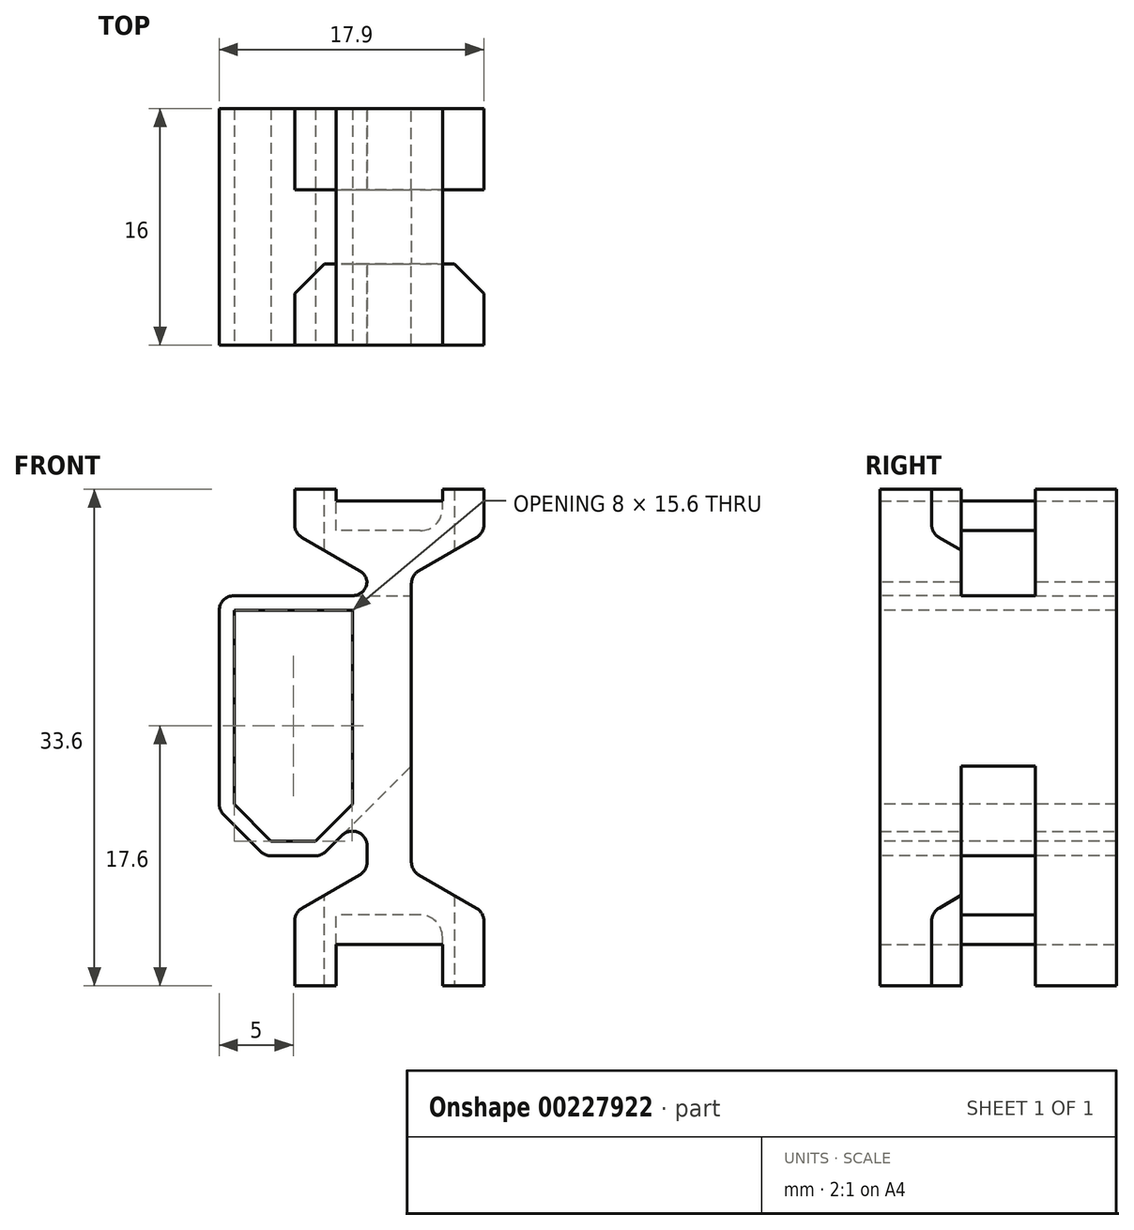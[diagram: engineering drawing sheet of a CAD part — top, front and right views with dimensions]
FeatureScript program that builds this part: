
annotation { "Feature Type Name" : "Feature", "Feature Type Description" : "" }
export const myFeature = defineFeature(function(context is Context, id is Id, definition is map)
    precondition{}
    {
        {
            var Q0;
            Q0=qCreatedBy(makeId("Front.planeOp"),FACE);
            var sketch = newSketch(context, id + "F0", { "sketchPlane" : qUnion([Q0])});
            skLineSegment(sketch, "E0.bottom", {"start": v(-6.4, 30.8) * mm, "end": v(-3.6, 30.8) * mm});
            skLineSegment(sketch, "E0.top", {"start": v(-6.4, -2.8) * mm, "end": v(-3.6, -2.8) * mm});
            skLineSegment(sketch, "E0.left", {"start": v(-6.4, 30.8) * mm, "end": v(-6.4, 27.83) * mm});
            skLineSegment(sketch, "E0.right", {"start": v(-3.6, 30.8) * mm, "end": v(-3.6, 30) * mm});
            skLineSegment(sketch, "E1.bottom", {"start": v(3.6, 30.8) * mm, "end": v(6.4, 30.8) * mm});
            skLineSegment(sketch, "E1.top", {"start": v(3.6, -2.8) * mm, "end": v(6.4, -2.8) * mm});
            skLineSegment(sketch, "E1.left", {"start": v(3.6, 30.8) * mm, "end": v(3.6, 30) * mm});
            skLineSegment(sketch, "E1.right", {"start": v(6.4, 30.8) * mm, "end": v(6.4, 27.83) * mm});
            skLineSegment(sketch, "E2.bottom", {"start": v(-3.6, 0) * mm, "end": v(3.6, 0) * mm});
            skLineSegment(sketch, "E2.top", {"start": v(-3.6, 30) * mm, "end": v(3.6, 30) * mm});
            skPoint(sketch, "E3", {"position": v(-5, 30.8) * mm});
            skPoint(sketch, "E4", {"position": v(5, 30.8) * mm});
            skLineSegment(sketch, "E5.trimOffspring", {"start": v(-6.4, 2.17) * mm, "end": v(-6.4, -2.8) * mm});
            skLineSegment(sketch, "E6.trimOffspring", {"start": v(-3.6, 0) * mm, "end": v(-3.6, -2.8) * mm});
            skLineSegment(sketch, "E7.trimOffspring", {"start": v(3.6, 0) * mm, "end": v(3.6, -2.8) * mm});
            skLineSegment(sketch, "E8", {"start": v(0, 30) * mm, "end": v(0, 0) * mm, "construction": true});
            skLineSegment(sketch, "E9", {"start": v(6.4, 15) * mm, "end": v(0, 15) * mm, "construction": true});
            skLineSegment(sketch, "E10", {"start": v(-6.4, 27.83) * mm, "end": v(-1.5, 25) * mm});
            skLineSegment(sketch, "E11", {"start": v(-1.5, 25) * mm, "end": v(-1.5, 5) * mm});
            skLineSegment(sketch, "E12", {"start": v(-1.5, 5) * mm, "end": v(-6.4, 2.17) * mm});
            skLineSegment(sketch, "E13.MirrorCS", {"start": v(1.5, 5) * mm, "end": v(6.4, 2.17) * mm});
            skLineSegment(sketch, "E14.MirrorCS", {"start": v(6.4, 27.83) * mm, "end": v(1.5, 25) * mm});
            skLineSegment(sketch, "E15.MirrorCS", {"start": v(1.5, 25) * mm, "end": v(1.5, 5) * mm});
            skLineSegment(sketch, "E16.trimOffspring", {"start": v(6.4, 2.17) * mm, "end": v(6.4, -2.8) * mm});
            skSolve(sketch);
        }
        {
            var Q0;
            Q0 = qSketchRegion(id + "F0", true);
            extrude(context, id + "F1", {"entities" : qUnion([Q0]), "depth" : 16 * mm});
        }
        {
            var Q0;
            Q0=makeQuery(id+"F1.opExtrude","SWEPT_FACE",FACE,{"disambiguationData":[OSD([sQuery(id+"F0.wireOp",EDGE,"E0.bottom")])]});
            var sketch = newSketch(context, id + "F2", { "sketchPlane" : qUnion([Q0])});
            skLineSegment(sketch, "E17", {"start": v(-6.4, -8) * mm, "end": v(6.4, -8) * mm, "construction": true});
            skLineSegment(sketch, "E18.0.1", {"start": v(-6.4, -5.5) * mm, "end": v(-6.4, -10.5) * mm});
            skLineSegment(sketch, "E18.0.3", {"start": v(-3.6, -10.5) * mm, "end": v(-3.6, -5.5) * mm});
            skLineSegment(sketch, "E19.0.1", {"start": v(3.6, -5.5) * mm, "end": v(3.6, -10.5) * mm});
            skLineSegment(sketch, "E19.0.3", {"start": v(6.4, -10.5) * mm, "end": v(6.4, -5.5) * mm});
            skLineSegment(sketch, "E20", {"start": v(-6.4, -5.5) * mm, "end": v(-3.6, -5.5) * mm});
            skLineSegment(sketch, "E21.MirrorCS", {"start": v(-6.4, -10.5) * mm, "end": v(-3.6, -10.5) * mm});
            skLineSegment(sketch, "E22.trimOffspring", {"start": v(3.6, -5.5) * mm, "end": v(6.4, -5.5) * mm});
            skLineSegment(sketch, "E23.trimOffspring", {"start": v(3.6, -10.5) * mm, "end": v(6.4, -10.5) * mm});
            skSolve(sketch);
        }
        {
            var Q0;
            Q0=makeQuery(id+"F2.imprint","IMPRINT",FACE,{"disambiguationData":[TD([[makeQuery(id+"F2.imprint","IMPRINT",EDGE,{"derivedFrom":sQuery(id+"F2.wireOp",EDGE,"E18.0.1")}),-1.0]])]});
            var Q1;
            Q1=makeQuery(id+"F2.imprint","IMPRINT",FACE,{"disambiguationData":[TD([[makeQuery(id+"F2.imprint","IMPRINT",EDGE,{"derivedFrom":sQuery(id+"F2.wireOp",EDGE,"E19.0.1")}),1.0]])]});
            extrude(context, id + "F3", {"entities" : qUnion([Q0, Q1]), "operationType" : NewBodyOperationType.REMOVE, "endBound" : BoundingType.THROUGH_ALL, "oppositeDirection" : true, "depth" : 25 * mm});
        }
        {
            var Q0;
            Q0=makeQuery(id+"F3.boolean.opBoolean","COPY",FACE,{"disambiguationData":[TD([makeQuery(id+"F1.opExtrude","SWEPT_FACE",FACE,{"disambiguationData":[OSD([sQuery(id+"F0.wireOp",EDGE,"E2.bottom")])]})])],"derivedFrom":makeQuery(id+"F3.opExtrude","SWEPT_FACE",FACE,{"disambiguationData":[OSD([sQuery(id+"F2.wireOp",EDGE,"E18.0.3")])]})});
            var sketch = newSketch(context, id + "F4", { "sketchPlane" : qUnion([Q0])});
            skLineSegment(sketch, "E24.bottom", {"start": v(5.5, 2) * mm, "end": v(10.5, 2) * mm});
            skLineSegment(sketch, "E24.top", {"start": v(5.5, 28) * mm, "end": v(10.5, 28) * mm});
            skLineSegment(sketch, "E24.left", {"start": v(5.5, 2) * mm, "end": v(5.5, 28) * mm});
            skLineSegment(sketch, "E24.right", {"start": v(10.5, 2) * mm, "end": v(10.5, 28) * mm});
            skSolve(sketch);
        }
        {
            var Q0;
            Q0 = qSketchRegion(id + "F4", true);
            extrude(context, id + "F5", {"entities" : qUnion([Q0]), "operationType" : NewBodyOperationType.REMOVE, "endBound" : BoundingType.THROUGH_ALL, "oppositeDirection" : true, "depth" : 25 * mm});
        }
        {
            var Q0;
            Q0=makeQuery(id+"F1.opExtrude","CAP_FACE",FACE,{"disambiguationData":[OSD([sQuery(id+"F0.wireOp",EDGE,"E0.bottom"),sQuery(id+"F0.wireOp",EDGE,"E0.top"),sQuery(id+"F0.wireOp",EDGE,"E0.left"),sQuery(id+"F0.wireOp",EDGE,"E0.right"),sQuery(id+"F0.wireOp",EDGE,"E1.bottom"),sQuery(id+"F0.wireOp",EDGE,"E1.top"),sQuery(id+"F0.wireOp",EDGE,"E1.left"),sQuery(id+"F0.wireOp",EDGE,"E1.right"),sQuery(id+"F0.wireOp",EDGE,"E2.bottom"),sQuery(id+"F0.wireOp",EDGE,"E2.top"),sQuery(id+"F0.wireOp",EDGE,"E5.trimOffspring"),sQuery(id+"F0.wireOp",EDGE,"E6.trimOffspring"),sQuery(id+"F0.wireOp",EDGE,"E7.trimOffspring"),sQuery(id+"F0.wireOp",EDGE,"XNyugLao-tsnu-Sah3-VUFn-nM4j8uXXMLVh"),sQuery(id+"F0.wireOp",EDGE,"qag7rgW7-rpCx-CGtA-zPlC-gOamsbcd0Z1q"),sQuery(id+"F0.wireOp",EDGE,"LMqOLITl-EVo5-MTzV-QNNo-kao2bXQrC091"),sQuery(id+"F0.wireOp",EDGE,"kiGqG5in-MVmp-Csza-V1P0-bwSz3CtIkC7l")])],"isStart":false});
            var sketch = newSketch(context, id + "F6", { "sketchPlane" : qUnion([Q0])});
            skLineSegment(sketch, "E25", {"start": v(-10.5, 22.6) * mm, "end": v(-10.5, 9.5) * mm});
            skLineSegment(sketch, "E26", {"start": v(-10.5, 9.5) * mm, "end": v(-8, 7) * mm});
            skLineSegment(sketch, "E27", {"start": v(-8, 7) * mm, "end": v(-5, 7) * mm});
            skLineSegment(sketch, "E28", {"start": v(-6.5, 7) * mm, "end": v(-6.5, 22.6) * mm, "construction": true});
            skLineSegment(sketch, "E29.0", {"start": v(-4.59, 6) * mm, "end": v(1.5, 12.09) * mm});
            skLineSegment(sketch, "E29.1", {"start": v(-11.5, 23.6) * mm, "end": v(-11.5, 23.6) * mm});
            skLineSegment(sketch, "E29.2", {"start": v(-11.5, 23.6) * mm, "end": v(-11.5, 9.09) * mm});
            skLineSegment(sketch, "E29.3", {"start": v(-11.5, 9.09) * mm, "end": v(-8.41, 6) * mm});
            skLineSegment(sketch, "E29.4", {"start": v(-8.41, 6) * mm, "end": v(-4.59, 6) * mm});
            skLineSegment(sketch, "E30", {"start": v(-11.5, 23.6) * mm, "end": v(1.5, 23.6) * mm});
            skLineSegment(sketch, "E31", {"start": v(1.5, 12.09) * mm, "end": v(1.5, 23.6) * mm});
            skLineSegment(sketch, "E32.MirrorCS", {"start": v(-2.5, 9.5) * mm, "end": v(-5, 7) * mm});
            skLineSegment(sketch, "E33.MirrorCS", {"start": v(-2.5, 22.6) * mm, "end": v(-2.5, 9.5) * mm});
            skLineSegment(sketch, "E34", {"start": v(-10.5, 22.6) * mm, "end": v(-2.5, 22.6) * mm});
            skSolve(sketch);
        }
        {
            var Q0;
            Q0 = qSketchRegion(id + "F6", true);
            var Q1;
            Q1=makeQuery(id+"F1.opExtrude","CAP_FACE",FACE,{"disambiguationData":[OSD([sQuery(id+"F0.wireOp",EDGE,"E0.bottom"),sQuery(id+"F0.wireOp",EDGE,"E0.top"),sQuery(id+"F0.wireOp",EDGE,"E0.left"),sQuery(id+"F0.wireOp",EDGE,"E0.right"),sQuery(id+"F0.wireOp",EDGE,"E1.bottom"),sQuery(id+"F0.wireOp",EDGE,"E1.top"),sQuery(id+"F0.wireOp",EDGE,"E1.left"),sQuery(id+"F0.wireOp",EDGE,"E1.right"),sQuery(id+"F0.wireOp",EDGE,"E2.bottom"),sQuery(id+"F0.wireOp",EDGE,"E2.top"),sQuery(id+"F0.wireOp",EDGE,"E5.trimOffspring"),sQuery(id+"F0.wireOp",EDGE,"E6.trimOffspring"),sQuery(id+"F0.wireOp",EDGE,"E7.trimOffspring"),sQuery(id+"F0.wireOp",EDGE,"XNyugLao-tsnu-Sah3-VUFn-nM4j8uXXMLVh"),sQuery(id+"F0.wireOp",EDGE,"qag7rgW7-rpCx-CGtA-zPlC-gOamsbcd0Z1q"),sQuery(id+"F0.wireOp",EDGE,"LMqOLITl-EVo5-MTzV-QNNo-kao2bXQrC091"),sQuery(id+"F0.wireOp",EDGE,"kiGqG5in-MVmp-Csza-V1P0-bwSz3CtIkC7l")])],"isStart":true});
            extrude(context, id + "F7", {"entities" : qUnion([Q0]), "operationType" : NewBodyOperationType.ADD, "endBound" : BoundingType.UP_TO_SURFACE, "oppositeDirection" : true, "endBoundEntityFace" : qUnion([Q1]), "depth" : 25 * mm});
        }
        {
            var Q0;
            Q0=makeQuery(id+"F5.boolean.opBoolean","INTERSECT",EDGE,{"derivedFrom":[makeQuery(id+"F3.boolean.opBoolean","COPY",FACE,{"disambiguationData":[TD([makeQuery(id+"F1.opExtrude","SWEPT_FACE",FACE,{"disambiguationData":[OSD([sQuery(id+"F0.wireOp",EDGE,"E2.bottom")])]})])],"derivedFrom":makeQuery(id+"F3.opExtrude","SWEPT_FACE",FACE,{"disambiguationData":[OSD([sQuery(id+"F2.wireOp",EDGE,"E19.0.1")])]})}),makeQuery(id+"F5.opExtrude","SWEPT_FACE",FACE,{"disambiguationData":[OSD([sQuery(id+"F4.wireOp",EDGE,"E24.bottom")])]})]});
            var Q1;
            Q1=makeQuery(id+"F5.boolean.opBoolean","INTERSECT",EDGE,{"derivedFrom":[makeQuery(id+"F3.boolean.opBoolean","COPY",FACE,{"disambiguationData":[TD([makeQuery(id+"F1.opExtrude","SWEPT_FACE",FACE,{"disambiguationData":[OSD([sQuery(id+"F0.wireOp",EDGE,"E1.left")])]})])],"derivedFrom":makeQuery(id+"F3.opExtrude","SWEPT_FACE",FACE,{"disambiguationData":[OSD([sQuery(id+"F2.wireOp",EDGE,"E19.0.1")])]})}),makeQuery(id+"F5.opExtrude","SWEPT_FACE",FACE,{"disambiguationData":[OSD([sQuery(id+"F4.wireOp",EDGE,"E24.top")])]})]});
            var Q2;
            Q2=makeQuery(id+"F5.boolean.opBoolean","COPY",EDGE,{"derivedFrom":makeQuery(id+"F5.opExtrude","CAP_EDGE",EDGE,{"disambiguationData":[OSD([sQuery(id+"F4.wireOp",EDGE,"E24.top")])],"isStart":true})});
            var Q3;
            Q3=makeQuery(id+"F5.boolean.opBoolean","COPY",EDGE,{"derivedFrom":makeQuery(id+"F5.opExtrude","CAP_EDGE",EDGE,{"disambiguationData":[OSD([sQuery(id+"F4.wireOp",EDGE,"E24.bottom")])],"isStart":true})});
            fillet(context, id + "F8", {"entities" : qUnion([Q0, Q1, Q2, Q3]), "radius" : 1.5 * mm, "tangentPropagation" : true, "allowEdgeOverflow" : false});
        }
        {
            var Q0;
            {var subQ0=sQuery(id+"F2.wireOp",EDGE,"E23.trimOffspring");Q0=makeQuery(id+"F3.boolean.opBoolean","COPY",EDGE,{"disambiguationData":[TD([makeQuery(id+"F1.opExtrude","SWEPT_FACE",FACE,{"disambiguationData":[OSD([sQuery(id+"F0.wireOp",EDGE,"E1.top")])]})])],"derivedFrom":makeQuery(id+"F3.opExtrude","SWEPT_EDGE",EDGE,{"disambiguationData":[OSD([sQuery(id+"F2.wireOp",EDGE,"E19.0.3"),subQ0])]})});}
            var Q1;
            {var subQ0=sQuery(id+"F2.wireOp",EDGE,"E22.trimOffspring");Q1=makeQuery(id+"F3.boolean.opBoolean","COPY",EDGE,{"disambiguationData":[TD([makeQuery(id+"F1.opExtrude","SWEPT_FACE",FACE,{"disambiguationData":[OSD([sQuery(id+"F0.wireOp",EDGE,"E1.top")])]})])],"derivedFrom":makeQuery(id+"F3.opExtrude","SWEPT_EDGE",EDGE,{"disambiguationData":[OSD([sQuery(id+"F2.wireOp",EDGE,"E19.0.3"),subQ0])]})});}
            var Q2;
            {var subQ0=sQuery(id+"F2.wireOp",EDGE,"E23.trimOffspring");Q2=makeQuery(id+"F3.boolean.opBoolean","COPY",EDGE,{"disambiguationData":[TD([makeQuery(id+"F1.opExtrude","SWEPT_FACE",FACE,{"disambiguationData":[OSD([sQuery(id+"F0.wireOp",EDGE,"E1.bottom")])]})])],"derivedFrom":makeQuery(id+"F3.opExtrude","SWEPT_EDGE",EDGE,{"disambiguationData":[OSD([sQuery(id+"F2.wireOp",EDGE,"E19.0.3"),subQ0])]})});}
            var Q3;
            {var subQ0=sQuery(id+"F2.wireOp",EDGE,"E22.trimOffspring");Q3=makeQuery(id+"F3.boolean.opBoolean","COPY",EDGE,{"disambiguationData":[TD([makeQuery(id+"F1.opExtrude","SWEPT_FACE",FACE,{"disambiguationData":[OSD([sQuery(id+"F0.wireOp",EDGE,"E1.bottom")])]})])],"derivedFrom":makeQuery(id+"F3.opExtrude","SWEPT_EDGE",EDGE,{"disambiguationData":[OSD([sQuery(id+"F2.wireOp",EDGE,"E19.0.3"),subQ0])]})});}
            var Q4;
            {var subQ0=sQuery(id+"F2.wireOp",EDGE,"E20");Q4=makeQuery(id+"F3.boolean.opBoolean","COPY",EDGE,{"disambiguationData":[TD([makeQuery(id+"F1.opExtrude","SWEPT_FACE",FACE,{"disambiguationData":[OSD([sQuery(id+"F0.wireOp",EDGE,"E0.top")])]})])],"derivedFrom":makeQuery(id+"F3.opExtrude","SWEPT_EDGE",EDGE,{"disambiguationData":[OSD([sQuery(id+"F0.wireOp",EDGE,"E0.bottom"),sQuery(id+"F0.wireOp",EDGE,"E0.left"),sQuery(id+"F2.wireOp",EDGE,"E18.0.1"),subQ0])]})});}
            var Q5;
            {var subQ0=sQuery(id+"F2.wireOp",EDGE,"E21.MirrorCS");Q5=makeQuery(id+"F3.boolean.opBoolean","COPY",EDGE,{"disambiguationData":[TD([makeQuery(id+"F1.opExtrude","SWEPT_FACE",FACE,{"disambiguationData":[OSD([sQuery(id+"F0.wireOp",EDGE,"E0.top")])]})])],"derivedFrom":makeQuery(id+"F3.opExtrude","SWEPT_EDGE",EDGE,{"disambiguationData":[OSD([sQuery(id+"F0.wireOp",EDGE,"E0.bottom"),sQuery(id+"F0.wireOp",EDGE,"E0.left"),sQuery(id+"F2.wireOp",EDGE,"E18.0.1"),subQ0])]})});}
            var Q6;
            {var subQ0=sQuery(id+"F0.wireOp",EDGE,"E0.bottom");var subQ1=sQuery(id+"F2.wireOp",EDGE,"E20");var subQ2=sQuery(id+"F0.wireOp",EDGE,"E0.left");Q6=makeQuery(id+"F3.boolean.opBoolean","COPY",EDGE,{"disambiguationData":[TD([makeQuery(id+"F1.opExtrude","SWEPT_FACE",FACE,{"disambiguationData":[OSD([subQ0])]})])],"derivedFrom":makeQuery(id+"F3.opExtrude","SWEPT_EDGE",EDGE,{"disambiguationData":[OSD([subQ0,subQ2,sQuery(id+"F2.wireOp",EDGE,"E18.0.1"),subQ1])]})});}
            var Q7;
            {var subQ0=sQuery(id+"F0.wireOp",EDGE,"E0.bottom");var subQ1=sQuery(id+"F2.wireOp",EDGE,"E21.MirrorCS");var subQ2=sQuery(id+"F0.wireOp",EDGE,"E0.left");Q7=makeQuery(id+"F3.boolean.opBoolean","COPY",EDGE,{"disambiguationData":[TD([makeQuery(id+"F1.opExtrude","SWEPT_FACE",FACE,{"disambiguationData":[OSD([subQ0])]})])],"derivedFrom":makeQuery(id+"F3.opExtrude","SWEPT_EDGE",EDGE,{"disambiguationData":[OSD([subQ0,subQ2,sQuery(id+"F2.wireOp",EDGE,"E18.0.1"),subQ1])]})});}
            chamfer(context, id + "F9", {"entities" : qUnion([Q0, Q1, Q2, Q3, Q4, Q5, Q6, Q7]), "width" : 2 * mm, "tangentPropagation" : true});
        }
        {
            var Q0;
            Q0=makeQuery(id+"F7.opExtrude","SWEPT_EDGE",EDGE,{"disambiguationData":[OSD([sQuery(id+"F6.wireOp",EDGE,"E29.2"),sQuery(id+"F6.wireOp",EDGE,"E30")])]});
            var Q1;
            Q1=makeQuery(id+"F7.opExtrude","SWEPT_EDGE",EDGE,{"disambiguationData":[OSD([sQuery(id+"F6.wireOp",EDGE,"E29.2"),sQuery(id+"F6.wireOp",EDGE,"E29.3")])]});
            var Q2;
            Q2=makeQuery(id+"F7.opExtrude","SWEPT_EDGE",EDGE,{"disambiguationData":[OSD([sQuery(id+"F6.wireOp",EDGE,"E29.3"),sQuery(id+"F6.wireOp",EDGE,"E29.4")])]});
            var Q3;
            Q3=makeQuery(id+"F7.opExtrude","SWEPT_EDGE",EDGE,{"disambiguationData":[OSD([sQuery(id+"F6.wireOp",EDGE,"E29.0"),sQuery(id+"F6.wireOp",EDGE,"E29.4")])]});
            var Q4;
            {var subQ19=sQuery(id+"F0.wireOp",EDGE,"E11");Q4=makeQuery(id+"F7.boolean.opBoolean","INTERSECT",EDGE,{"derivedFrom":[makeQuery(id+"F5.boolean.opBoolean","SPLIT",FACE,{"disambiguationData":[TD([makeQuery(id+"F5.opExtrude","SWEPT_FACE",FACE,{"disambiguationData":[OSD([sQuery(id+"F4.wireOp",EDGE,"E24.right")])]})])],"derivedFrom":makeQuery(id+"F1.opExtrude","SWEPT_FACE",FACE,{"disambiguationData":[OSD([subQ19])]})}),makeQuery(id+"F7.opExtrude","SWEPT_FACE",FACE,{"disambiguationData":[OSD([sQuery(id+"F6.wireOp",EDGE,"E29.0")])]})]});}
            var Q5;
            {var subQ20=sQuery(id+"F0.wireOp",EDGE,"E11");Q5=makeQuery(id+"F7.boolean.opBoolean","INTERSECT",EDGE,{"derivedFrom":[makeQuery(id+"F5.boolean.opBoolean","SPLIT",FACE,{"disambiguationData":[TD([makeQuery(id+"F5.opExtrude","SWEPT_FACE",FACE,{"disambiguationData":[OSD([sQuery(id+"F4.wireOp",EDGE,"E24.left")])]})])],"derivedFrom":makeQuery(id+"F1.opExtrude","SWEPT_FACE",FACE,{"disambiguationData":[OSD([subQ20])]})}),makeQuery(id+"F7.opExtrude","SWEPT_FACE",FACE,{"disambiguationData":[OSD([sQuery(id+"F6.wireOp",EDGE,"E29.0")])]})]});}
            var Q6;
            {var subQ19=sQuery(id+"F0.wireOp",EDGE,"E11");Q6=makeQuery(id+"F7.boolean.opBoolean","INTERSECT",EDGE,{"derivedFrom":[makeQuery(id+"F5.boolean.opBoolean","SPLIT",FACE,{"disambiguationData":[TD([makeQuery(id+"F5.opExtrude","SWEPT_FACE",FACE,{"disambiguationData":[OSD([sQuery(id+"F4.wireOp",EDGE,"E24.right")])]})])],"derivedFrom":makeQuery(id+"F1.opExtrude","SWEPT_FACE",FACE,{"disambiguationData":[OSD([subQ19])]})}),makeQuery(id+"F7.opExtrude","SWEPT_FACE",FACE,{"disambiguationData":[OSD([sQuery(id+"F6.wireOp",EDGE,"E30")])]})]});}
            var Q7;
            {var subQ20=sQuery(id+"F0.wireOp",EDGE,"E11");Q7=makeQuery(id+"F7.boolean.opBoolean","INTERSECT",EDGE,{"derivedFrom":[makeQuery(id+"F5.boolean.opBoolean","SPLIT",FACE,{"disambiguationData":[TD([makeQuery(id+"F5.opExtrude","SWEPT_FACE",FACE,{"disambiguationData":[OSD([sQuery(id+"F4.wireOp",EDGE,"E24.left")])]})])],"derivedFrom":makeQuery(id+"F1.opExtrude","SWEPT_FACE",FACE,{"disambiguationData":[OSD([subQ20])]})}),makeQuery(id+"F7.opExtrude","SWEPT_FACE",FACE,{"disambiguationData":[OSD([sQuery(id+"F6.wireOp",EDGE,"E30")])]})]});}
            var Q8;
            {var subQ0=sQuery(id+"F0.wireOp",EDGE,"E12");var subQ1=sQuery(id+"F0.wireOp",EDGE,"E5.trimOffspring");Q8=makeQuery(id+"F3.boolean.opBoolean","SPLIT",EDGE,{"disambiguationData":[TD([makeQuery(id+"F3.opExtrude","SWEPT_FACE",FACE,{"disambiguationData":[OSD([sQuery(id+"F2.wireOp",EDGE,"E21.MirrorCS")])]})])],"derivedFrom":makeQuery(id+"F1.opExtrude","SWEPT_EDGE",EDGE,{"disambiguationData":[OSD([subQ1,subQ0])]})});}
            var Q9;
            {var subQ0=sQuery(id+"F0.wireOp",EDGE,"E12");var subQ1=sQuery(id+"F0.wireOp",EDGE,"E5.trimOffspring");Q9=makeQuery(id+"F3.boolean.opBoolean","SPLIT",EDGE,{"disambiguationData":[TD([makeQuery(id+"F3.opExtrude","SWEPT_FACE",FACE,{"disambiguationData":[OSD([sQuery(id+"F2.wireOp",EDGE,"E20")])]})])],"derivedFrom":makeQuery(id+"F1.opExtrude","SWEPT_EDGE",EDGE,{"disambiguationData":[OSD([subQ1,subQ0])]})});}
            var Q10;
            {var subQ0=sQuery(id+"F0.wireOp",EDGE,"E10");var subQ1=sQuery(id+"F0.wireOp",EDGE,"E0.left");Q10=makeQuery(id+"F3.boolean.opBoolean","SPLIT",EDGE,{"disambiguationData":[TD([makeQuery(id+"F3.opExtrude","SWEPT_FACE",FACE,{"disambiguationData":[OSD([sQuery(id+"F2.wireOp",EDGE,"E21.MirrorCS")])]})])],"derivedFrom":makeQuery(id+"F1.opExtrude","SWEPT_EDGE",EDGE,{"disambiguationData":[OSD([subQ1,subQ0])]})});}
            var Q11;
            {var subQ0=sQuery(id+"F0.wireOp",EDGE,"E10");var subQ1=sQuery(id+"F0.wireOp",EDGE,"E0.left");Q11=makeQuery(id+"F3.boolean.opBoolean","SPLIT",EDGE,{"disambiguationData":[TD([makeQuery(id+"F3.opExtrude","SWEPT_FACE",FACE,{"disambiguationData":[OSD([sQuery(id+"F2.wireOp",EDGE,"E20")])]})])],"derivedFrom":makeQuery(id+"F1.opExtrude","SWEPT_EDGE",EDGE,{"disambiguationData":[OSD([subQ1,subQ0])]})});}
            var Q12;
            {var subQ0=sQuery(id+"F0.wireOp",EDGE,"E14.MirrorCS");var subQ1=sQuery(id+"F0.wireOp",EDGE,"E1.right");Q12=makeQuery(id+"F3.boolean.opBoolean","SPLIT",EDGE,{"disambiguationData":[TD([makeQuery(id+"F3.opExtrude","SWEPT_FACE",FACE,{"disambiguationData":[OSD([sQuery(id+"F2.wireOp",EDGE,"E23.trimOffspring")])]})])],"derivedFrom":makeQuery(id+"F1.opExtrude","SWEPT_EDGE",EDGE,{"disambiguationData":[OSD([subQ1,subQ0])]})});}
            var Q13;
            {var subQ0=sQuery(id+"F0.wireOp",EDGE,"E14.MirrorCS");var subQ1=sQuery(id+"F0.wireOp",EDGE,"E1.right");Q13=makeQuery(id+"F3.boolean.opBoolean","SPLIT",EDGE,{"disambiguationData":[TD([makeQuery(id+"F3.opExtrude","SWEPT_FACE",FACE,{"disambiguationData":[OSD([sQuery(id+"F2.wireOp",EDGE,"E22.trimOffspring")])]})])],"derivedFrom":makeQuery(id+"F1.opExtrude","SWEPT_EDGE",EDGE,{"disambiguationData":[OSD([subQ1,subQ0])]})});}
            var Q14;
            {var subQ0=sQuery(id+"F0.wireOp",EDGE,"E16.trimOffspring");var subQ1=sQuery(id+"F0.wireOp",EDGE,"E13.MirrorCS");Q14=makeQuery(id+"F3.boolean.opBoolean","SPLIT",EDGE,{"disambiguationData":[TD([makeQuery(id+"F3.opExtrude","SWEPT_FACE",FACE,{"disambiguationData":[OSD([sQuery(id+"F2.wireOp",EDGE,"E23.trimOffspring")])]})])],"derivedFrom":makeQuery(id+"F1.opExtrude","SWEPT_EDGE",EDGE,{"disambiguationData":[OSD([subQ1,subQ0])]})});}
            var Q15;
            {var subQ0=sQuery(id+"F0.wireOp",EDGE,"E16.trimOffspring");var subQ1=sQuery(id+"F0.wireOp",EDGE,"E13.MirrorCS");Q15=makeQuery(id+"F3.boolean.opBoolean","SPLIT",EDGE,{"disambiguationData":[TD([makeQuery(id+"F3.opExtrude","SWEPT_FACE",FACE,{"disambiguationData":[OSD([sQuery(id+"F2.wireOp",EDGE,"E22.trimOffspring")])]})])],"derivedFrom":makeQuery(id+"F1.opExtrude","SWEPT_EDGE",EDGE,{"disambiguationData":[OSD([subQ1,subQ0])]})});}
            var Q16;
            {var subQ8=sQuery(id+"F0.wireOp",EDGE,"E15.MirrorCS");var subQ9=sQuery(id+"F0.wireOp",EDGE,"E13.MirrorCS");Q16=makeQuery(id+"F5.boolean.opBoolean","SPLIT",EDGE,{"disambiguationData":[TD([makeQuery(id+"F5.opExtrude","SWEPT_FACE",FACE,{"disambiguationData":[OSD([sQuery(id+"F4.wireOp",EDGE,"E24.right")])]})])],"derivedFrom":makeQuery(id+"F1.opExtrude","SWEPT_EDGE",EDGE,{"disambiguationData":[OSD([subQ9,subQ8])]})});}
            var Q17;
            {var subQ8=sQuery(id+"F0.wireOp",EDGE,"E15.MirrorCS");var subQ11=sQuery(id+"F0.wireOp",EDGE,"E13.MirrorCS");Q17=makeQuery(id+"F5.boolean.opBoolean","SPLIT",EDGE,{"disambiguationData":[TD([makeQuery(id+"F5.opExtrude","SWEPT_FACE",FACE,{"disambiguationData":[OSD([sQuery(id+"F4.wireOp",EDGE,"E24.left")])]})])],"derivedFrom":makeQuery(id+"F1.opExtrude","SWEPT_EDGE",EDGE,{"disambiguationData":[OSD([subQ11,subQ8])]})});}
            var Q18;
            {var subQ8=sQuery(id+"F0.wireOp",EDGE,"E15.MirrorCS");var subQ10=sQuery(id+"F0.wireOp",EDGE,"E14.MirrorCS");Q18=makeQuery(id+"F5.boolean.opBoolean","SPLIT",EDGE,{"disambiguationData":[TD([makeQuery(id+"F5.opExtrude","SWEPT_FACE",FACE,{"disambiguationData":[OSD([sQuery(id+"F4.wireOp",EDGE,"E24.left")])]})])],"derivedFrom":makeQuery(id+"F1.opExtrude","SWEPT_EDGE",EDGE,{"disambiguationData":[OSD([subQ10,subQ8])]})});}
            var Q19;
            {var subQ8=sQuery(id+"F0.wireOp",EDGE,"E15.MirrorCS");var subQ9=sQuery(id+"F0.wireOp",EDGE,"E14.MirrorCS");Q19=makeQuery(id+"F5.boolean.opBoolean","SPLIT",EDGE,{"disambiguationData":[TD([makeQuery(id+"F5.opExtrude","SWEPT_FACE",FACE,{"disambiguationData":[OSD([sQuery(id+"F4.wireOp",EDGE,"E24.right")])]})])],"derivedFrom":makeQuery(id+"F1.opExtrude","SWEPT_EDGE",EDGE,{"disambiguationData":[OSD([subQ9,subQ8])]})});}
            var Q20;
            {var subQ8=sQuery(id+"F0.wireOp",EDGE,"E12");var subQ18=sQuery(id+"F0.wireOp",EDGE,"E11");Q20=makeQuery(id+"F5.boolean.opBoolean","SPLIT",EDGE,{"disambiguationData":[TD([makeQuery(id+"F5.opExtrude","SWEPT_FACE",FACE,{"disambiguationData":[OSD([sQuery(id+"F4.wireOp",EDGE,"E24.left")])]})])],"derivedFrom":makeQuery(id+"F1.opExtrude","SWEPT_EDGE",EDGE,{"disambiguationData":[OSD([subQ18,subQ8])]})});}
            var Q21;
            {var subQ8=sQuery(id+"F0.wireOp",EDGE,"E11");var subQ17=sQuery(id+"F0.wireOp",EDGE,"E12");Q21=makeQuery(id+"F5.boolean.opBoolean","SPLIT",EDGE,{"disambiguationData":[TD([makeQuery(id+"F5.opExtrude","SWEPT_FACE",FACE,{"disambiguationData":[OSD([sQuery(id+"F4.wireOp",EDGE,"E24.right")])]})])],"derivedFrom":makeQuery(id+"F1.opExtrude","SWEPT_EDGE",EDGE,{"disambiguationData":[OSD([subQ8,subQ17])]})});}
            var Q22;
            {var subQ5=sQuery(id+"F0.wireOp",EDGE,"E10");var subQ9=sQuery(id+"F0.wireOp",EDGE,"E11");Q22=makeQuery(id+"F5.boolean.opBoolean","SPLIT",EDGE,{"disambiguationData":[TD([makeQuery(id+"F5.opExtrude","SWEPT_FACE",FACE,{"disambiguationData":[OSD([sQuery(id+"F4.wireOp",EDGE,"E24.right")])]})])],"derivedFrom":makeQuery(id+"F1.opExtrude","SWEPT_EDGE",EDGE,{"disambiguationData":[OSD([subQ5,subQ9])]})});}
            var Q23;
            {var subQ5=sQuery(id+"F0.wireOp",EDGE,"E10");var subQ9=sQuery(id+"F0.wireOp",EDGE,"E11");Q23=makeQuery(id+"F5.boolean.opBoolean","SPLIT",EDGE,{"disambiguationData":[TD([makeQuery(id+"F5.opExtrude","SWEPT_FACE",FACE,{"disambiguationData":[OSD([sQuery(id+"F4.wireOp",EDGE,"E24.left")])]})])],"derivedFrom":makeQuery(id+"F1.opExtrude","SWEPT_EDGE",EDGE,{"disambiguationData":[OSD([subQ5,subQ9])]})});}
            fillet(context, id + "F10", {"entities" : qUnion([Q0, Q1, Q2, Q3, Q4, Q5, Q6, Q7, Q8, Q9, Q10, Q11, Q12, Q13, Q14, Q15, Q16, Q17, Q18, Q19, Q20, Q21, Q22, Q23]), "radius" : 1 * mm, "tangentPropagation" : true, "allowEdgeOverflow" : false});
        }
    });
